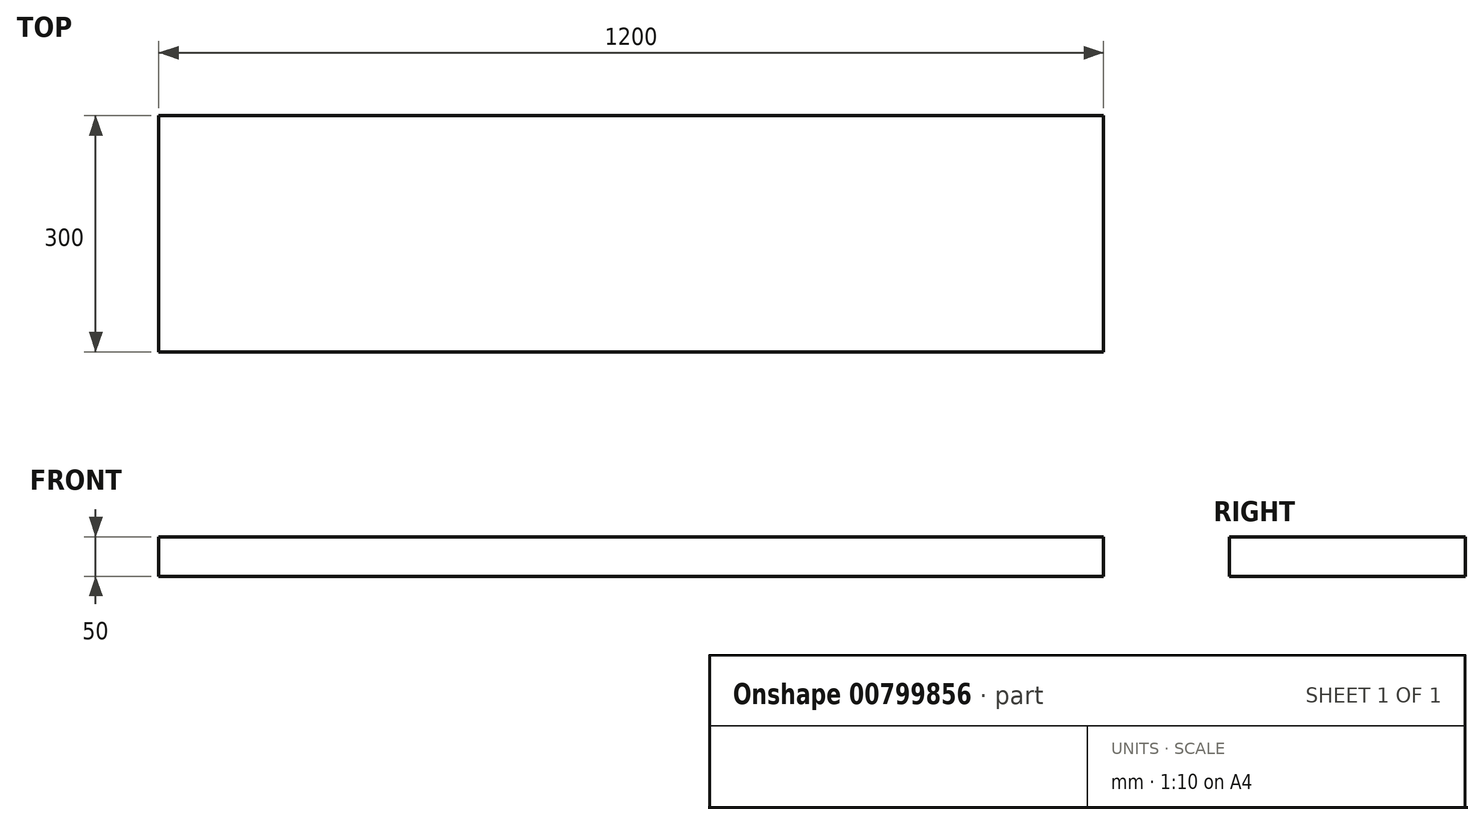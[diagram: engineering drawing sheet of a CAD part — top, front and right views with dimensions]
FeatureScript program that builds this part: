
annotation { "Feature Type Name" : "Feature", "Feature Type Description" : "" }
export const myFeature = defineFeature(function(context is Context, id is Id, definition is map)
    precondition{}
    {
        {
            var Q0;
            Q0=qCreatedBy(makeId("Top.planeOp"),FACE);
            var sketch = newSketch(context, id + "F0", { "sketchPlane" : qUnion([Q0])});
            skLineSegment(sketch, "E0", {"start": v(0, 0) * mm, "end": v(0, 0) * mm});
            skLineSegment(sketch, "E1", {"start": v(0, 0) * mm, "end": v(-400, 0) * mm});
            skLineSegment(sketch, "E2", {"start": v(-400, 0) * mm, "end": v(-400, 300) * mm});
            skLineSegment(sketch, "E3", {"start": v(-400, 300) * mm, "end": v(800, 300) * mm});
            skLineSegment(sketch, "E4", {"start": v(800, 300) * mm, "end": v(800, 0) * mm});
            skLineSegment(sketch, "E5", {"start": v(800, 0) * mm, "end": v(0, 0) * mm});
            skSolve(sketch);
        }
        {
            var Q0;
            Q0=makeQuery(id+"F0.imprint","IMPRINT",FACE,{"disambiguationData":[TD([[makeQuery(id+"F0.imprint","IMPRINT",EDGE,{"derivedFrom":sQuery(id+"F0.wireOp",EDGE,"E1")}),-1.0]])]});
            extrude(context, id + "F1", {"entities" : qUnion([Q0]), "depth" : 50 * mm, "offsetDistance" : 25 * mm});
        }
    });
